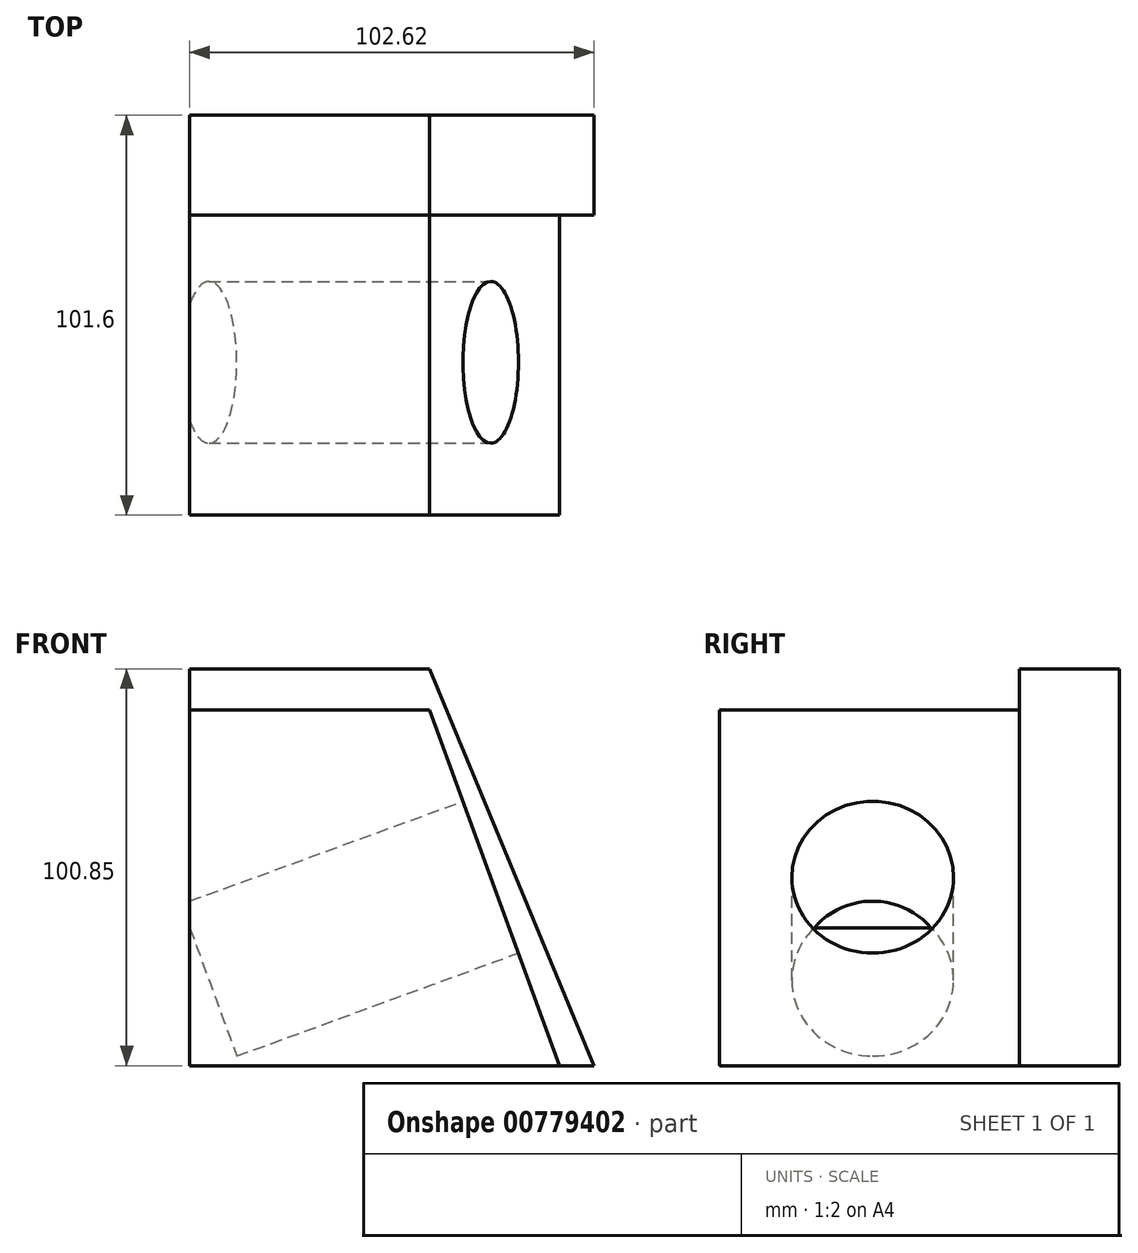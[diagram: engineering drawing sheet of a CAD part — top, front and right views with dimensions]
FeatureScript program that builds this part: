
annotation { "Feature Type Name" : "Feature", "Feature Type Description" : "" }
export const myFeature = defineFeature(function(context is Context, id is Id, definition is map)
    precondition{}
    {
        {
            var Q0;
            Q0=qCreatedBy(makeId("Front.planeOp"),FACE);
            var sketch = newSketch(context, id + "F0", { "sketchPlane" : qUnion([Q0])});
            skLineSegment(sketch, "E0", {"start": v(-65.6, 55.89) * mm, "end": v(-65.6, -34.5) * mm});
            skLineSegment(sketch, "E1", {"start": v(-65.6, -34.5) * mm, "end": v(28.35, -34.5) * mm});
            skLineSegment(sketch, "E2", {"start": v(28.35, -34.5) * mm, "end": v(-4.7, 55.89) * mm});
            skLineSegment(sketch, "E3", {"start": v(-4.7, 55.89) * mm, "end": v(-65.6, 55.89) * mm});
            skLineSegment(sketch, "E4", {"start": v(-65.6, 55.89) * mm, "end": v(-65.6, 66.36) * mm});
            skLineSegment(sketch, "E5", {"start": v(-65.6, 66.36) * mm, "end": v(-4.7, 66.36) * mm});
            skLineSegment(sketch, "E6", {"start": v(-4.7, 66.36) * mm, "end": v(37.02, -34.5) * mm});
            skLineSegment(sketch, "E7", {"start": v(37.02, -34.5) * mm, "end": v(28.35, -34.5) * mm});
            skSolve(sketch);
        }
        {
            var Q0;
            Q0=makeQuery(id+"F0.imprint","IMPRINT",FACE,{"disambiguationData":[TD([[makeQuery(id+"F0.imprint","IMPRINT",EDGE,{"derivedFrom":sQuery(id+"F0.wireOp",EDGE,"E0")}),1.0]])]});
            extrude(context, id + "F1", {"entities" : qUnion([Q0]), "depth" : 76.2 * mm, "offsetDistance" : 25.4 * mm});
        }
        {
            var Q0;
            Q0 = qSketchRegion(id + "F0", true);
            extrude(context, id + "F2", {"entities" : qUnion([Q0]), "operationType" : NewBodyOperationType.ADD, "oppositeDirection" : true, "depth" : 25.4 * mm, "offsetDistance" : 25.4 * mm});
        }
        {
            var Q0;
            Q0=makeQuery(id+"F1.opExtrude","SWEPT_FACE",FACE,{"disambiguationData":[OSD([sQuery(id+"F0.wireOp",EDGE,"E2")])]});
            var sketch = newSketch(context, id + "F3", { "sketchPlane" : qUnion([Q0])});
            skCircle(sketch, "E8", {"center": v(-37.34, 8.86) * mm, "radius": 20.54 * mm});
            skSolve(sketch);
        }
        {
            var Q0;
            Q0 = qSketchRegion(id + "F3", true);
            extrude(context, id + "F4", {"entities" : qUnion([Q0]), "operationType" : NewBodyOperationType.REMOVE, "oppositeDirection" : true, "depth" : 76.2 * mm, "offsetDistance" : 25.4 * mm});
        }
    });
